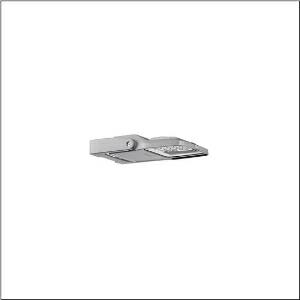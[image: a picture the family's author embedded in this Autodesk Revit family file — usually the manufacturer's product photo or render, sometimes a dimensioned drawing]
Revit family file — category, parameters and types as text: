
# Revit family: floodlight_fl_21_iq_micro___pl52_5xa7761a2d2a_1372
name_source: partatom
category: Lighting Fixtures
units: mm (PartAtom-declared; Revit-internal decimal feet)

## family parameters
Cut with Voids When Loaded = No
Host = Face
Light Source = No
Part Type = Normal
Room Calculation Point = No
Round Connector Dimension = Use Diameter
Shared = No

## types (1)
- --- (1 x LED, 2890 lm, 23.1 W, 3000K)
    Apparent Load = 23 VA
    CIE Flux Codes = 26 60 98 100 100
    Color Rendering = 70
    Color Temperature = 3000K
    Default Elevation = 1800 mm
    Description = Floodlight FL 21 iQ micro, floodlight, primary light control with lens, of PMMA, primary optical cover: protective disc, of toughened safety glass, transparent, light distribution: PL52, light emission: direct distribution, installation type: surface-mounted, LED, High Power LED, rated luminous flux: 2.890lm, luminous efficacy: 125lm/W, light colour: 730, colour temperature: 3000K, control gear: iQ Comfort/DALI, control: optimised constant luminous flux control (CLO 2.0), Desk-Remote (wireless, voltage-free reading and setting of iQ features in the workshop via application-optimized NFC function/RFID function), Light-Fading, Smart-Wire, Night-Set, Lumen-Switch, Temp-Guard, Auto-Match, with terminal, 6-pole, mains connection: 220..240V, AC, 50/60Hz, start of lifetime: 23W, end of service life: 24W, reduction: 11W, luminaire housing, of diecast aluminium, powder-coated, Siteco® metallic grey (DB 702S), corrosivity category C5 mid according to DIN EN ISO 12944, suitable for swimming pools, chlorine-resistant, sealing non-destructively replaceable, design bracket, of diecast aluminium, powder-coated, Siteco® metallic grey (DB 702S), protection rating (complete): IP66, insulation class (complete): insulation class II (safety insulation), certification: CE, ENEC, VDE, protection symbol: D, impact resistance: IK07, permissible operating ambient temperature: -40..+40°C, permissible operating ambient temperature for outdoor applications: -40..+50°C, standard: DIN EN 12944, LABS conformity tested according to VDMA 24364:2018-05, packaging unit: 1 piece

Light Distribution: PL52
    Height = 65 mm
    Lamp = 1 x LED
    Lamp Light Flux = 2890 lm
    Lamp Power = 23.1 W
    Lamp count = 1
    Length = 312 mm
    Luminous efficacy = 125 lm/W
    Manufacturer = Siteco
    ModVariant = No
    Model = 5XA7761A2D2A
    Mounting Place = Wall
    Mounting Type = Surface mounted
    Number of Poles = 1
    OnlyDefault = Yes
    Power Factor = 1
    Product Name = Floodlight FL 21 iQ micro | PL52
    Product group = floodlight | wall mounted
    ProductGroupID = 2001
    Protection Class = Protection class II
    Protection Degree = IP 66
    RLX_Detail_Level = 1
    RLX_Emergency_Light_Flux = 0 lm
    RLX_Emergency_Type = 0
    RLX_Emergency_Type_DB = No
    RlxData = <blob elided: 97493 chars, md5=ef0ff0ee>
    Socket = socket
    Standby Power = 0 W
    System Light Flux = 2890 lm
    System Power = 23 W
    Type Comments = factory setting: luminous flux: 100 % | dim-lin: 254 | 455 mA
    Type Image = l_1006878.jpg
    URL = http://relux.com
    VarID = @adj_199603
    Voltage = 0 V
    Weight = 0.00 kg
    Width = 230 mm

## geometry (parser evidence)
native form markers: Blend x4, Sweep x12
no freeform markers — native parametric forms only
